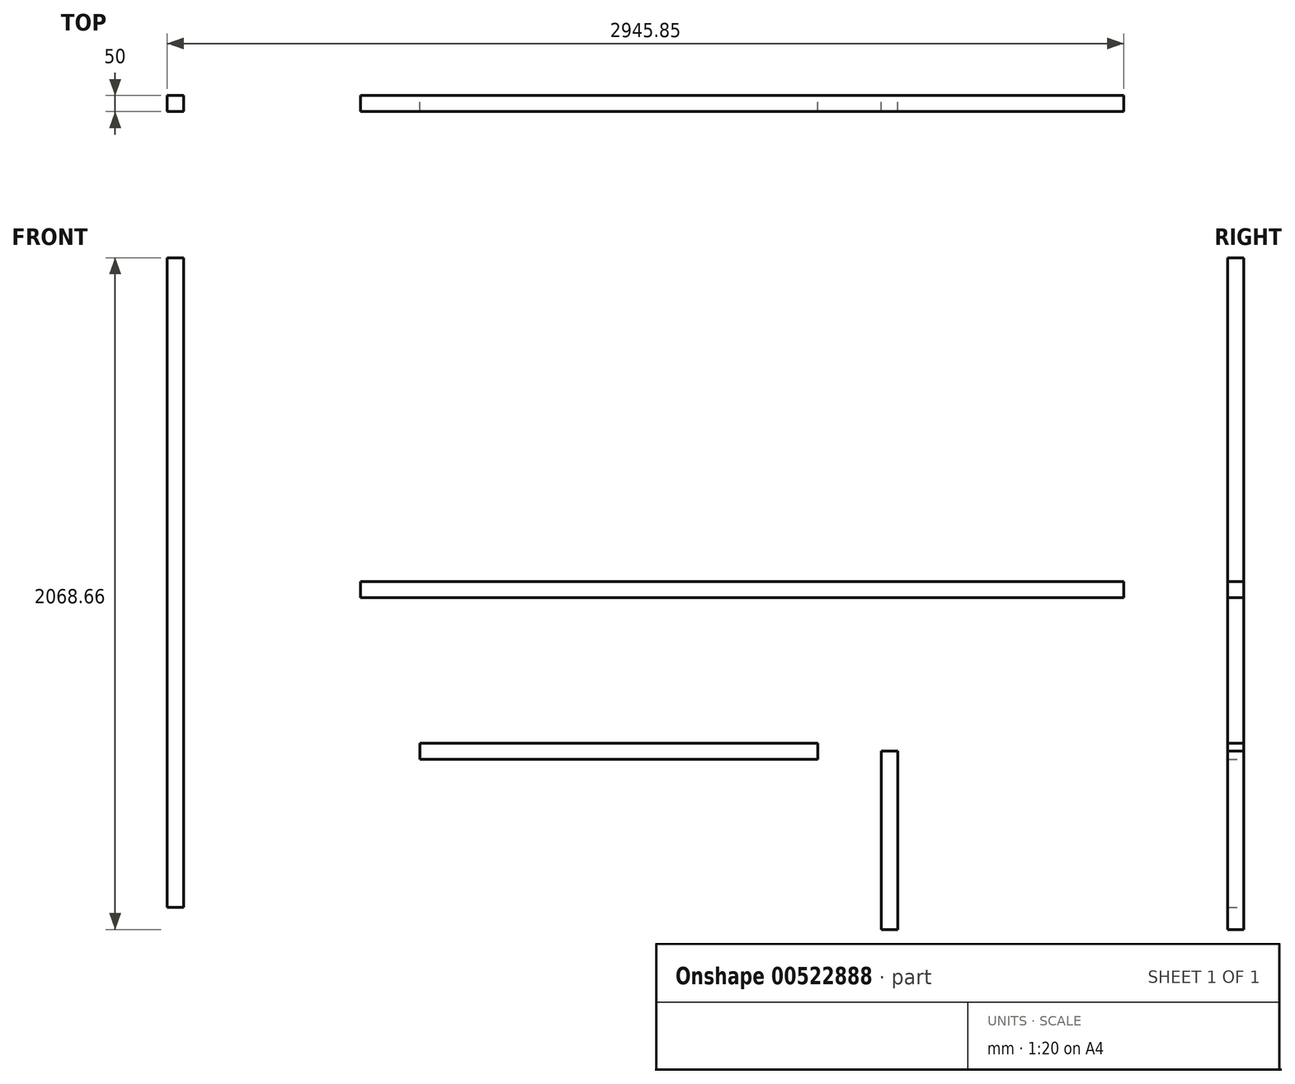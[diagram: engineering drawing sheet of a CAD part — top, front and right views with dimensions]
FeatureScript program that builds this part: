
annotation { "Feature Type Name" : "Feature", "Feature Type Description" : "" }
export const myFeature = defineFeature(function(context is Context, id is Id, definition is map)
    precondition{}
    {
        {
            var Q0;
            Q0=qCreatedBy(makeId("Front.planeOp"),FACE);
            var sketch = newSketch(context, id + "F0", { "sketchPlane" : qUnion([Q0])});
            skLineSegment(sketch, "E0", {"start": v(-327.05, 51.31) * mm, "end": v(2022.95, 51.31) * mm});
            skLineSegment(sketch, "E1", {"start": v(2022.95, 51.31) * mm, "end": v(2022.95, 1.31) * mm});
            skLineSegment(sketch, "E2", {"start": v(2022.95, 1.31) * mm, "end": v(-327.05, 1.31) * mm});
            skLineSegment(sketch, "E3", {"start": v(-327.05, 1.31) * mm, "end": v(-327.05, 51.31) * mm});
            skLineSegment(sketch, "E4", {"start": v(-922.9, 1048.5) * mm, "end": v(-872.9, 1048.5) * mm});
            skLineSegment(sketch, "E5", {"start": v(-872.9, 1048.5) * mm, "end": v(-872.9, -951.5) * mm});
            skLineSegment(sketch, "E6", {"start": v(-872.9, -951.5) * mm, "end": v(-922.9, -951.5) * mm});
            skLineSegment(sketch, "E7", {"start": v(-922.9, -951.5) * mm, "end": v(-922.9, 1048.5) * mm});
            skLineSegment(sketch, "E8", {"start": v(-144.65, -446.67) * mm, "end": v(1080.35, -446.67) * mm});
            skLineSegment(sketch, "E9", {"start": v(1080.35, -446.67) * mm, "end": v(1080.35, -496.67) * mm});
            skLineSegment(sketch, "E10", {"start": v(1080.35, -496.67) * mm, "end": v(-144.65, -496.67) * mm});
            skLineSegment(sketch, "E11", {"start": v(-144.65, -496.67) * mm, "end": v(-144.65, -446.67) * mm});
            skLineSegment(sketch, "E12", {"start": v(1276.73, -470.17) * mm, "end": v(1326.73, -470.17) * mm});
            skLineSegment(sketch, "E13", {"start": v(1326.73, -470.17) * mm, "end": v(1326.73, -1020.17) * mm});
            skLineSegment(sketch, "E14", {"start": v(1326.73, -1020.17) * mm, "end": v(1276.73, -1020.17) * mm});
            skLineSegment(sketch, "E15", {"start": v(1276.73, -1020.17) * mm, "end": v(1276.73, -470.17) * mm});
            skSolve(sketch);
        }
        {
            var Q0;
            Q0=makeQuery(id+"F0.imprint","IMPRINT",FACE,{"disambiguationData":[TD([[makeQuery(id+"F0.imprint","IMPRINT",EDGE,{"derivedFrom":sQuery(id+"F0.wireOp",EDGE,"E0")}),-1.0]])]});
            var Q1;
            Q1=makeQuery(id+"F0.imprint","IMPRINT",FACE,{"disambiguationData":[TD([[makeQuery(id+"F0.imprint","IMPRINT",EDGE,{"derivedFrom":sQuery(id+"F0.wireOp",EDGE,"E4")}),-1.0]])]});
            var Q2;
            Q2=makeQuery(id+"F0.imprint","IMPRINT",FACE,{"disambiguationData":[TD([[makeQuery(id+"F0.imprint","IMPRINT",EDGE,{"derivedFrom":sQuery(id+"F0.wireOp",EDGE,"E8")}),-1.0]])]});
            var Q3;
            Q3=makeQuery(id+"F0.imprint","IMPRINT",FACE,{"disambiguationData":[TD([[makeQuery(id+"F0.imprint","IMPRINT",EDGE,{"derivedFrom":sQuery(id+"F0.wireOp",EDGE,"E12")}),-1.0]])]});
            extrude(context, id + "F1", {"entities" : qUnion([Q0, Q1, Q2, Q3]), "depth" : 50 * mm, "offsetDistance" : 25 * mm});
        }
    });
